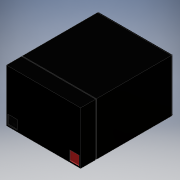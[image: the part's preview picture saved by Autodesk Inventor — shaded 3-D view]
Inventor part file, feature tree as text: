
AUTODESK INVENTOR PART (.ipt)
format: ipt  version: 2016 (Build 200138000, 138)  size: 172,544 bytes
history: native  units: mm
features: extrude x4, sketch x4, fillet x3
ambient origin geometry x8: Origin, YZ Plane, XZ Plane, XY Plane, X Axis, Y Axis, Z Axis, Center Point
bodies: Solid1 (feature_tree)
feature tree (11):
  extrude  "Extrusion1"  Depth=79.0mm
  extrude  "Extrusion2"  Depth=0.5mm
  extrude  "Extrusion3"  Depth=0.5mm
  fillet  "Fillet1"  Radius=0.5mm
  extrude  "Extrusion4"  Depth=16.0mm TaperAngle=0.0deg
  fillet  "Fillet2"  Radius=2.0mm
  fillet  "Fillet3"  Radius=10.0mm
  sketch  "Sketch1"  dims[d0=56.0mm d1=79.0mm]
  sketch  "Sketch4"  dims[d2=82.0mm d3=0.0mm d4=0.5mm]
  sketch  "Sketch5"  dims[d5=0.5mm d7=0.5mm d8=0.5mm]
  sketch  "Sketch6"  dims[d9=1.0mm d10=0.0mm d11=16.0mm d12=0.0mm d13=2.0mm d14=10.0mm d15=10.0mm d16=1.5mm d17=1.5mm d18=10.0mm d19=10.0mm d20=1.5mm d21=1.5mm d22=0.5mm d23=0.0mm d24=0.5mm d25=0.5mm]
